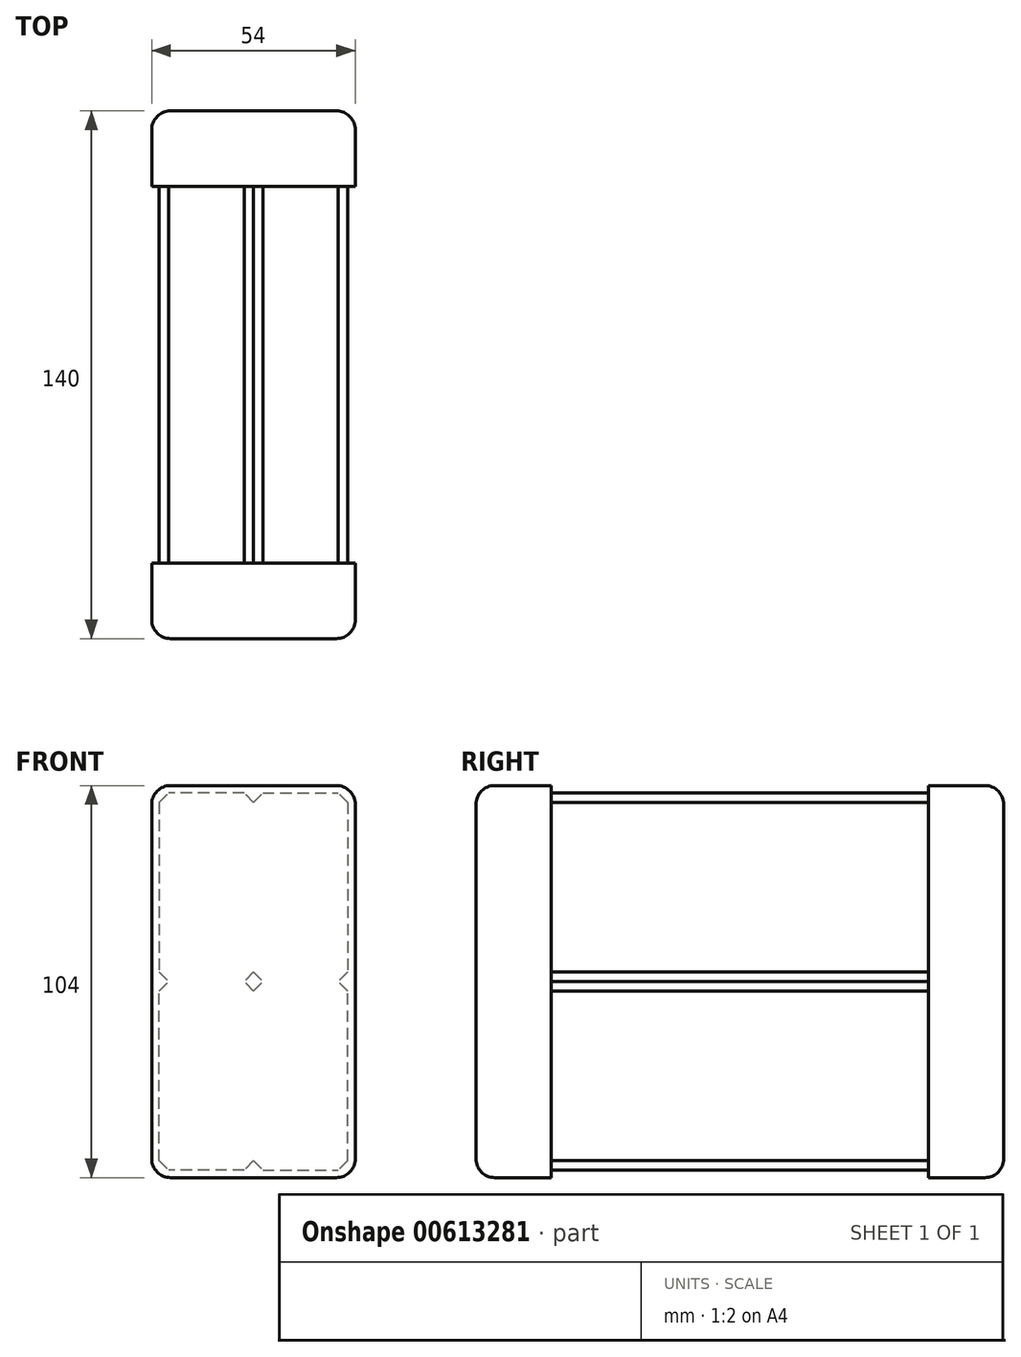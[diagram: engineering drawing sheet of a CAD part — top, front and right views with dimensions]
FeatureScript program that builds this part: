
annotation { "Feature Type Name" : "Feature", "Feature Type Description" : "" }
export const myFeature = defineFeature(function(context is Context, id is Id, definition is map)
    precondition{}
    {
        {
            var Q0;
            Q0=qCreatedBy(makeId("Right.planeOp"),FACE);
            var sketch = newSketch(context, id + "F0", { "sketchPlane" : qUnion([Q0])});
            skLineSegment(sketch, "E0.bottom", {"start": v(0, 0) * mm, "end": v(50, 0) * mm});
            skLineSegment(sketch, "E0.top", {"start": v(0, 50) * mm, "end": v(50, 50) * mm});
            skLineSegment(sketch, "E0.left", {"start": v(0, 0) * mm, "end": v(0, 50) * mm});
            skLineSegment(sketch, "E0.right", {"start": v(50, 0) * mm, "end": v(50, 50) * mm});
            skSolve(sketch);
        }
        {
            var Q0;
            Q0 = qSketchRegion(id + "F0", true);
            extrude(context, id + "F1", {"entities" : qUnion([Q0]), "depth" : 25 * mm, "offsetDistance" : 25 * mm});
        }
        {
            var Q0;
            Q0=makeQuery(id+"F1.opExtrude","CAP_EDGE",EDGE,{"disambiguationData":[OSD([sQuery(id+"F0.wireOp",EDGE,"E0.top")])],"isStart":false});
            var Q1;
            Q1=makeQuery(id+"F1.opExtrude","CAP_EDGE",EDGE,{"disambiguationData":[OSD([sQuery(id+"F0.wireOp",EDGE,"E0.top")])],"isStart":true});
            var Q2;
            Q2=makeQuery(id+"F1.opExtrude","CAP_EDGE",EDGE,{"disambiguationData":[OSD([sQuery(id+"F0.wireOp",EDGE,"E0.bottom")])],"isStart":false});
            var Q3;
            Q3=makeQuery(id+"F1.opExtrude","CAP_EDGE",EDGE,{"disambiguationData":[OSD([sQuery(id+"F0.wireOp",EDGE,"E0.bottom")])],"isStart":true});
            chamfer(context, id + "F2", {"entities" : qUnion([Q0, Q1, Q2, Q3]), "width" : 2.5 * mm, "tangentPropagation" : true});
        }
        {
            var Q0;
            Q0=makeQuery(id+"F1.opExtrude","SWEPT_BODY",BODY,{"disambiguationData":[OSD([sQuery(id+"F0.wireOp",EDGE,"E0.bottom"),sQuery(id+"F0.wireOp",EDGE,"E0.top"),sQuery(id+"F0.wireOp",EDGE,"E0.left"),sQuery(id+"F0.wireOp",EDGE,"E0.right")])]});
            var Q1;
            Q1=makeQuery(id+"F1.opExtrude","SWEPT_FACE",FACE,{"disambiguationData":[OSD([sQuery(id+"F0.wireOp",EDGE,"E0.top")])]});
            mirror(context, id + "F3", {"operationType" : NewBodyOperationType.ADD, "entities" : qUnion([Q0]), "mirrorPlane" : qUnion([Q1])});
        }
        {
            var Q0;
            Q0=makeQuery(id+"F1.opExtrude","SWEPT_BODY",BODY,{"disambiguationData":[OSD([sQuery(id+"F0.wireOp",EDGE,"E0.bottom"),sQuery(id+"F0.wireOp",EDGE,"E0.top"),sQuery(id+"F0.wireOp",EDGE,"E0.left"),sQuery(id+"F0.wireOp",EDGE,"E0.right")])]});
            var Q1;
            Q1=makeQuery(id+"F3.opPattern","COPY",FACE,{"derivedFrom":makeQuery(id+"F1.opExtrude","CAP_FACE",FACE,{"disambiguationData":[OSD([sQuery(id+"F0.wireOp",EDGE,"E0.bottom"),sQuery(id+"F0.wireOp",EDGE,"E0.top"),sQuery(id+"F0.wireOp",EDGE,"E0.left"),sQuery(id+"F0.wireOp",EDGE,"E0.right")])],"isStart":false}),"instanceName":"1"});
            mirror(context, id + "F4", {"operationType" : NewBodyOperationType.ADD, "entities" : qUnion([Q0]), "mirrorPlane" : qUnion([Q1])});
        }
        {
            var Q0;
            {var subQ0=makeQuery(id+"F1.opExtrude","SWEPT_FACE",FACE,{"disambiguationData":[OSD([sQuery(id+"F0.wireOp",EDGE,"E0.right")])]});var subQ1=makeQuery(id+"F3.boolean.opBoolean","MERGE",FACE,{"derivedFrom":[subQ0,makeQuery(id+"F3.opPattern","COPY",FACE,{"derivedFrom":subQ0,"instanceName":"1"})]});Q0=makeQuery(id+"F4.boolean.opBoolean","MERGE",FACE,{"derivedFrom":[subQ1,makeQuery(id+"F4.opPattern","COPY",FACE,{"derivedFrom":subQ1,"instanceName":"1"})]});}
            var sketch = newSketch(context, id + "F5", { "sketchPlane" : qUnion([Q0])});
            skLineSegment(sketch, "E1.bottom", {"start": v(-52, 102) * mm, "end": v(2, 102) * mm});
            skLineSegment(sketch, "E1.top", {"start": v(-52, -2) * mm, "end": v(2, -2) * mm});
            skLineSegment(sketch, "E1.left", {"start": v(-52, 102) * mm, "end": v(-52, -2) * mm});
            skLineSegment(sketch, "E1.right", {"start": v(2, 102) * mm, "end": v(2, -2) * mm});
            skSolve(sketch);
        }
        {
            var Q0;
            Q0 = qSketchRegion(id + "F5", true);
            extrude(context, id + "F6", {"entities" : qUnion([Q0]), "operationType" : NewBodyOperationType.ADD, "depth" : 20 * mm, "offsetDistance" : 25 * mm});
        }
        {
            var Q0;
            Q0=makeQuery(id+"F6.opExtrude","CAP_FACE",FACE,{"disambiguationData":[OSD([sQuery(id+"F5.wireOp",EDGE,"E1.bottom"),sQuery(id+"F5.wireOp",EDGE,"E1.top"),sQuery(id+"F5.wireOp",EDGE,"E1.left"),sQuery(id+"F5.wireOp",EDGE,"E1.right")])],"isStart":false});
            var Q1;
            Q1=makeQuery(id+"F6.opExtrude","SWEPT_EDGE",EDGE,{"disambiguationData":[OSD([sQuery(id+"F5.wireOp",EDGE,"E1.top"),sQuery(id+"F5.wireOp",EDGE,"E1.right")])]});
            var Q2;
            Q2=makeQuery(id+"F6.opExtrude","SWEPT_EDGE",EDGE,{"disambiguationData":[OSD([sQuery(id+"F5.wireOp",EDGE,"E1.bottom"),sQuery(id+"F5.wireOp",EDGE,"E1.right")])]});
            var Q3;
            Q3=makeQuery(id+"F6.opExtrude","SWEPT_EDGE",EDGE,{"disambiguationData":[OSD([sQuery(id+"F5.wireOp",EDGE,"E1.bottom"),sQuery(id+"F5.wireOp",EDGE,"E1.left")])]});
            var Q4;
            Q4=makeQuery(id+"F6.opExtrude","SWEPT_EDGE",EDGE,{"disambiguationData":[OSD([sQuery(id+"F5.wireOp",EDGE,"E1.top"),sQuery(id+"F5.wireOp",EDGE,"E1.left")])]});
            fillet(context, id + "F7", {"entities" : qUnion([Q0, Q1, Q2, Q3, Q4]), "radius" : 5 * mm, "tangentPropagation" : true, "allowEdgeOverflow" : false});
        }
        {
            var Q0;
            Q0=makeQuery(id+"F1.opExtrude","SWEPT_BODY",BODY,{"disambiguationData":[OSD([sQuery(id+"F0.wireOp",EDGE,"E0.bottom"),sQuery(id+"F0.wireOp",EDGE,"E0.top"),sQuery(id+"F0.wireOp",EDGE,"E0.left"),sQuery(id+"F0.wireOp",EDGE,"E0.right")])]});
            var Q1;
            {var subQ0=makeQuery(id+"F1.opExtrude","SWEPT_FACE",FACE,{"disambiguationData":[OSD([sQuery(id+"F0.wireOp",EDGE,"E0.left")])]});var subQ1=makeQuery(id+"F3.boolean.opBoolean","MERGE",FACE,{"derivedFrom":[subQ0,makeQuery(id+"F3.opPattern","COPY",FACE,{"derivedFrom":subQ0,"instanceName":"1"})]});Q1=makeQuery(id+"F4.boolean.opBoolean","MERGE",FACE,{"derivedFrom":[subQ1,makeQuery(id+"F4.opPattern","COPY",FACE,{"derivedFrom":subQ1,"instanceName":"1"})]});}
            mirror(context, id + "F8", {"operationType" : NewBodyOperationType.ADD, "entities" : qUnion([Q0]), "mirrorPlane" : qUnion([Q1])});
        }
    });
